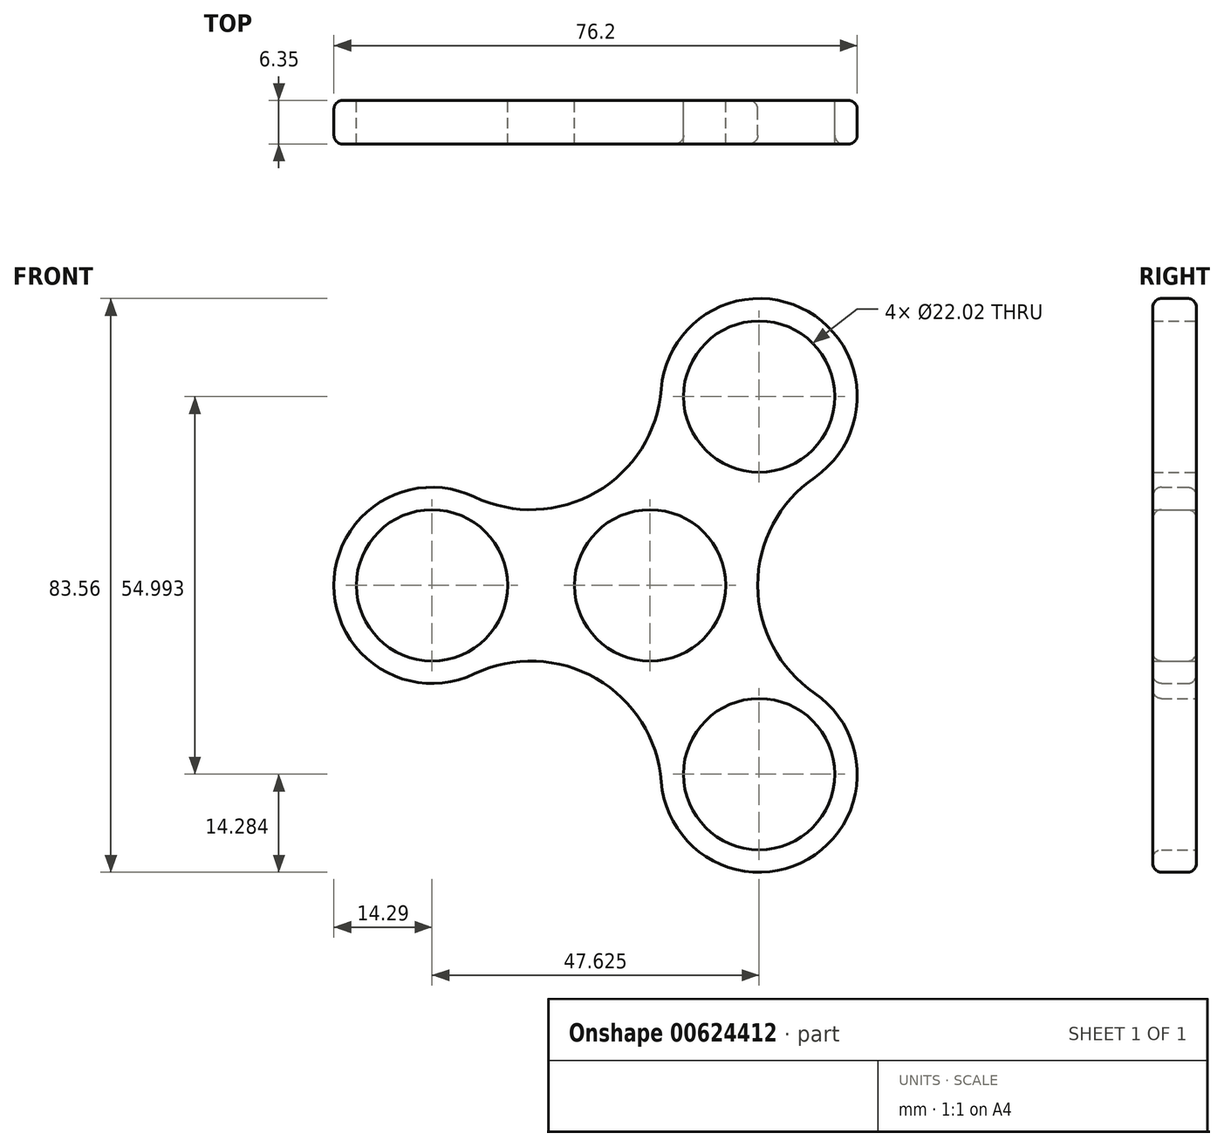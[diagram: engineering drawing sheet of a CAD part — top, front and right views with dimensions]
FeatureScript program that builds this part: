
annotation { "Feature Type Name" : "Feature", "Feature Type Description" : "" }
export const myFeature = defineFeature(function(context is Context, id is Id, definition is map)
    precondition{}
    {
        {
            var Q0;
            Q0=qCreatedBy(makeId("Front.planeOp"),FACE);
            var sketch = newSketch(context, id + "F0", { "sketchPlane" : qUnion([Q0])});
            skArc(sketch, "E0", {"start": v(-25.58, 12.89) * mm, "mid": v(-7.84, 13.58) * mm, "end": v(1.63, 28.6) * mm});
            skArc(sketch, "E1", {"start": v(23.95, 15.71) * mm, "mid": v(15.68, 0) * mm, "end": v(23.95, -15.71) * mm});
            skArc(sketch, "E2", {"start": v(1.63, -28.6) * mm, "mid": v(-7.84, -13.58) * mm, "end": v(-25.58, -12.89) * mm});
            skCircle(sketch, "E3.0", {"center": v(-31.75, 0) * mm, "radius": 11.01 * mm});
            skCircle(sketch, "E4.0", {"center": v(-31.75, 0) * mm, "radius": 14.29 * mm});
            skCircle(sketch, "E5.0", {"center": v(0, 0) * mm, "radius": 11.01 * mm});
            skCircle(sketch, "E6.0", {"center": v(15.88, 27.5) * mm, "radius": 14.29 * mm});
            skCircle(sketch, "E7.0", {"center": v(15.88, 27.5) * mm, "radius": 11.01 * mm});
            skCircle(sketch, "E8.0", {"center": v(15.87, -27.5) * mm, "radius": 14.29 * mm});
            skCircle(sketch, "E9.0", {"center": v(15.87, -27.5) * mm, "radius": 11.01 * mm});
            skSolve(sketch);
        }
        {
            var Q0;
            Q0 = qSketchRegion(id + "F0", true);
            extrude(context, id + "F1", {"entities" : qUnion([Q0]), "depth" : 6.35 * mm, "offsetDistance" : 25.4 * mm});
        }
        {
            var Q0;
            Q0=makeQuery(id+"F1.opExtrude","CAP_EDGE",EDGE,{"disambiguationData":[OSD([sQuery(id+"F0.wireOp",EDGE,"E4.0")])],"isStart":true});
            var Q1;
            Q1=makeQuery(id+"F1.opExtrude","CAP_EDGE",EDGE,{"disambiguationData":[OSD([sQuery(id+"F0.wireOp",EDGE,"E4.0")])],"isStart":false});
            var Q2;
            Q2=makeQuery(id+"F1.opExtrude","CAP_EDGE",EDGE,{"disambiguationData":[OSD([sQuery(id+"F0.wireOp",EDGE,"E0")])],"isStart":false});
            var Q3;
            Q3=makeQuery(id+"F1.opExtrude","CAP_EDGE",EDGE,{"disambiguationData":[OSD([sQuery(id+"F0.wireOp",EDGE,"E0")])],"isStart":true});
            var Q4;
            Q4=makeQuery(id+"F1.opExtrude","CAP_EDGE",EDGE,{"disambiguationData":[OSD([sQuery(id+"F0.wireOp",EDGE,"E6.0")])],"isStart":true});
            var Q5;
            Q5=makeQuery(id+"F1.opExtrude","CAP_EDGE",EDGE,{"disambiguationData":[OSD([sQuery(id+"F0.wireOp",EDGE,"E6.0")])],"isStart":false});
            var Q6;
            Q6=makeQuery(id+"F1.opExtrude","CAP_EDGE",EDGE,{"disambiguationData":[OSD([sQuery(id+"F0.wireOp",EDGE,"E2")])],"isStart":false});
            var Q7;
            Q7=makeQuery(id+"F1.opExtrude","CAP_EDGE",EDGE,{"disambiguationData":[OSD([sQuery(id+"F0.wireOp",EDGE,"E1")])],"isStart":false});
            var Q8;
            Q8=makeQuery(id+"F1.opExtrude","CAP_EDGE",EDGE,{"disambiguationData":[OSD([sQuery(id+"F0.wireOp",EDGE,"E1")])],"isStart":true});
            var Q9;
            Q9=makeQuery(id+"F1.opExtrude","CAP_EDGE",EDGE,{"disambiguationData":[OSD([sQuery(id+"F0.wireOp",EDGE,"E8.0")])],"isStart":true});
            var Q10;
            Q10=makeQuery(id+"F1.opExtrude","CAP_EDGE",EDGE,{"disambiguationData":[OSD([sQuery(id+"F0.wireOp",EDGE,"E9.0")])],"isStart":false});
            var Q11;
            Q11=makeQuery(id+"F1.opExtrude","CAP_EDGE",EDGE,{"disambiguationData":[OSD([sQuery(id+"F0.wireOp",EDGE,"E8.0")])],"isStart":false});
            var Q12;
            Q12=makeQuery(id+"F1.opExtrude","CAP_EDGE",EDGE,{"disambiguationData":[OSD([sQuery(id+"F0.wireOp",EDGE,"E2")])],"isStart":true});
            fillet(context, id + "F2", {"entities" : qUnion([Q0, Q1, Q2, Q3, Q4, Q5, Q6, Q7, Q8, Q9, Q10, Q11, Q12]), "radius" : 1.27 * mm, "tangentPropagation" : true, "allowEdgeOverflow" : false});
        }
    });
